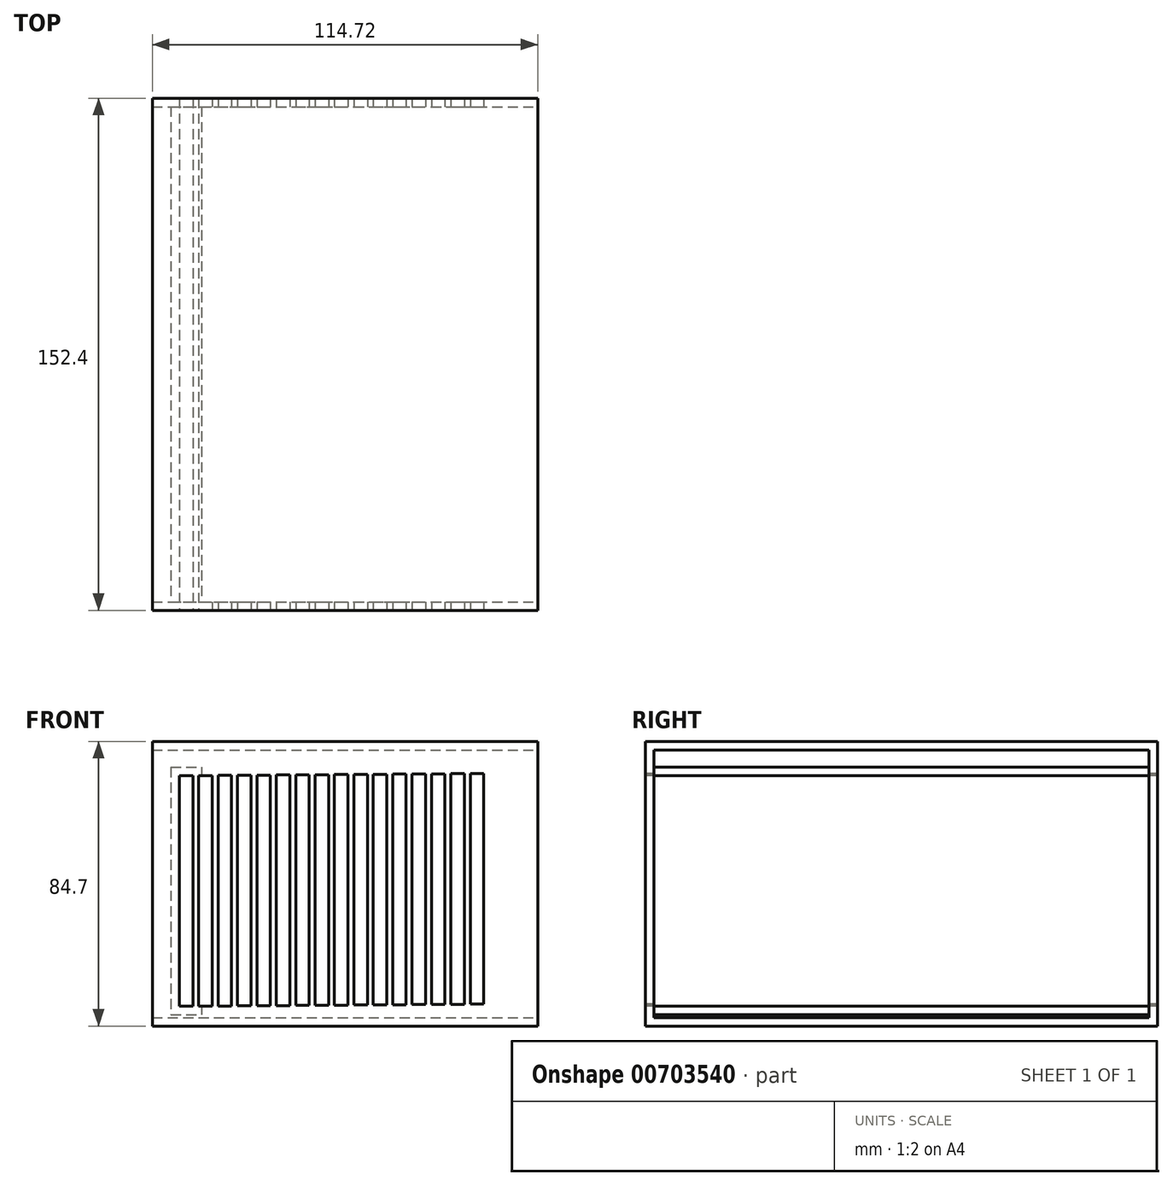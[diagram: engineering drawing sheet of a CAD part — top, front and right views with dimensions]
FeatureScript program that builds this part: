
annotation { "Feature Type Name" : "Feature", "Feature Type Description" : "" }
export const myFeature = defineFeature(function(context is Context, id is Id, definition is map)
    precondition{}
    {
        {
            var Q0;
            Q0=qCreatedBy(makeId("Front.planeOp"),FACE);
            var sketch = newSketch(context, id + "F0", { "sketchPlane" : qUnion([Q0])});
            skLineSegment(sketch, "E0.bottom", {"start": v(-56.22, 44.16) * mm, "end": v(58.5, 44.16) * mm});
            skLineSegment(sketch, "E0.top", {"start": v(-56.22, -40.54) * mm, "end": v(58.5, -40.54) * mm});
            skLineSegment(sketch, "E0.left", {"start": v(-56.22, 44.16) * mm, "end": v(-56.22, -40.54) * mm});
            skLineSegment(sketch, "E0.right", {"start": v(58.5, 44.16) * mm, "end": v(58.5, -40.54) * mm});
            skSolve(sketch);
        }
        {
            var Q0;
            Q0 = qSketchRegion(id + "F0", true);
            extrude(context, id + "F1", {"entities" : qUnion([Q0]), "depth" : 152.4 * mm, "offsetDistance" : 25.4 * mm});
        }
        {
            var Q0;
            Q0=makeQuery(id+"F1.opExtrude","CAP_FACE",FACE,{"disambiguationData":[OSD([sQuery(id+"F0.wireOp",EDGE,"E0.bottom"),sQuery(id+"F0.wireOp",EDGE,"E0.top"),sQuery(id+"F0.wireOp",EDGE,"E0.left"),sQuery(id+"F0.wireOp",EDGE,"E0.right")])],"isStart":false});
            var sketch = newSketch(context, id + "F2", { "sketchPlane" : qUnion([Q0])});
            skLineSegment(sketch, "E1.bottom", {"start": v(-48.18, 33.97) * mm, "end": v(-44.16, 33.97) * mm});
            skLineSegment(sketch, "E1.top", {"start": v(-48.18, -34.64) * mm, "end": v(-44.16, -34.64) * mm});
            skLineSegment(sketch, "E1.left", {"start": v(-48.18, 33.97) * mm, "end": v(-48.18, -34.64) * mm});
            skLineSegment(sketch, "E1.right", {"start": v(-44.16, 33.97) * mm, "end": v(-44.16, -34.64) * mm});
            skLineSegment(sketch, "E2.bottom", {"start": v(-2.01, 34.3) * mm, "end": v(2.01, 34.3) * mm});
            skLineSegment(sketch, "E2.top", {"start": v(-2.01, -34.3) * mm, "end": v(2.01, -34.3) * mm});
            skLineSegment(sketch, "E2.left", {"start": v(-2.01, 34.3) * mm, "end": v(-2.01, -34.3) * mm});
            skLineSegment(sketch, "E2.right", {"start": v(2.01, 34.3) * mm, "end": v(2.01, -34.3) * mm});
            skLineSegment(sketch, "E3.bottom", {"start": v(-25.1, 34.14) * mm, "end": v(-21.07, 34.14) * mm});
            skLineSegment(sketch, "E3.top", {"start": v(-25.1, -34.48) * mm, "end": v(-21.07, -34.48) * mm});
            skLineSegment(sketch, "E3.left", {"start": v(-25.1, 34.14) * mm, "end": v(-25.1, -34.48) * mm});
            skLineSegment(sketch, "E3.right", {"start": v(-21.07, 34.14) * mm, "end": v(-21.07, -34.48) * mm});
            skLineSegment(sketch, "E4.bottom", {"start": v(21.07, 34.48) * mm, "end": v(25.1, 34.48) * mm});
            skLineSegment(sketch, "E4.top", {"start": v(21.07, -34.14) * mm, "end": v(25.1, -34.14) * mm});
            skLineSegment(sketch, "E4.left", {"start": v(21.07, 34.48) * mm, "end": v(21.07, -34.14) * mm});
            skLineSegment(sketch, "E4.right", {"start": v(25.1, 34.48) * mm, "end": v(25.1, -34.14) * mm});
            skLineSegment(sketch, "E5.bottom", {"start": v(-36.64, 34.06) * mm, "end": v(-32.62, 34.06) * mm});
            skLineSegment(sketch, "E5.top", {"start": v(-36.64, -34.56) * mm, "end": v(-32.62, -34.56) * mm});
            skLineSegment(sketch, "E5.left", {"start": v(-36.64, 34.06) * mm, "end": v(-36.64, -34.56) * mm});
            skLineSegment(sketch, "E5.right", {"start": v(-32.62, 34.06) * mm, "end": v(-32.62, -34.56) * mm});
            skLineSegment(sketch, "E6.bottom", {"start": v(9.53, 34.4) * mm, "end": v(13.55, 34.4) * mm});
            skLineSegment(sketch, "E6.top", {"start": v(9.53, -34.23) * mm, "end": v(13.55, -34.23) * mm});
            skLineSegment(sketch, "E6.left", {"start": v(9.53, 34.4) * mm, "end": v(9.53, -34.23) * mm});
            skLineSegment(sketch, "E6.right", {"start": v(13.55, 34.4) * mm, "end": v(13.55, -34.23) * mm});
            skLineSegment(sketch, "E7.bottom", {"start": v(-13.55, 34.23) * mm, "end": v(-9.53, 34.23) * mm});
            skLineSegment(sketch, "E7.top", {"start": v(-13.55, -34.4) * mm, "end": v(-9.53, -34.4) * mm});
            skLineSegment(sketch, "E7.left", {"start": v(-13.55, 34.23) * mm, "end": v(-13.55, -34.4) * mm});
            skLineSegment(sketch, "E7.right", {"start": v(-9.53, 34.23) * mm, "end": v(-9.53, -34.4) * mm});
            skLineSegment(sketch, "E8.bottom", {"start": v(32.62, 34.56) * mm, "end": v(36.64, 34.56) * mm});
            skLineSegment(sketch, "E8.top", {"start": v(32.62, -34.06) * mm, "end": v(36.64, -34.06) * mm});
            skLineSegment(sketch, "E8.left", {"start": v(32.62, 34.56) * mm, "end": v(32.62, -34.06) * mm});
            skLineSegment(sketch, "E8.right", {"start": v(36.64, 34.56) * mm, "end": v(36.64, -34.06) * mm});
            skLineSegment(sketch, "E9.bottom", {"start": v(-42.4, 34.02) * mm, "end": v(-38.39, 34.02) * mm});
            skLineSegment(sketch, "E9.top", {"start": v(-42.4, -34.6) * mm, "end": v(-38.39, -34.6) * mm});
            skLineSegment(sketch, "E9.left", {"start": v(-42.4, 34.02) * mm, "end": v(-42.4, -34.6) * mm});
            skLineSegment(sketch, "E9.right", {"start": v(-38.39, 34.02) * mm, "end": v(-38.39, -34.6) * mm});
            skLineSegment(sketch, "E10.bottom", {"start": v(3.76, 34.35) * mm, "end": v(7.78, 34.35) * mm});
            skLineSegment(sketch, "E10.top", {"start": v(3.76, -34.27) * mm, "end": v(7.78, -34.27) * mm});
            skLineSegment(sketch, "E10.left", {"start": v(3.76, 34.35) * mm, "end": v(3.76, -34.27) * mm});
            skLineSegment(sketch, "E10.right", {"start": v(7.78, 34.35) * mm, "end": v(7.78, -34.27) * mm});
            skLineSegment(sketch, "E11.bottom", {"start": v(-19.32, 34.18) * mm, "end": v(-15.3, 34.18) * mm});
            skLineSegment(sketch, "E11.top", {"start": v(-19.32, -34.43) * mm, "end": v(-15.3, -34.43) * mm});
            skLineSegment(sketch, "E11.left", {"start": v(-19.32, 34.18) * mm, "end": v(-19.32, -34.43) * mm});
            skLineSegment(sketch, "E11.right", {"start": v(-15.3, 34.18) * mm, "end": v(-15.3, -34.43) * mm});
            skLineSegment(sketch, "E12.bottom", {"start": v(26.85, 34.52) * mm, "end": v(30.87, 34.52) * mm});
            skLineSegment(sketch, "E12.top", {"start": v(26.85, -34.1) * mm, "end": v(30.87, -34.1) * mm});
            skLineSegment(sketch, "E12.left", {"start": v(26.85, 34.52) * mm, "end": v(26.85, -34.1) * mm});
            skLineSegment(sketch, "E12.right", {"start": v(30.87, 34.52) * mm, "end": v(30.87, -34.1) * mm});
            skLineSegment(sketch, "E13.bottom", {"start": v(-30.87, 34.1) * mm, "end": v(-26.85, 34.1) * mm});
            skLineSegment(sketch, "E13.top", {"start": v(-30.87, -34.52) * mm, "end": v(-26.85, -34.52) * mm});
            skLineSegment(sketch, "E13.left", {"start": v(-30.87, 34.1) * mm, "end": v(-30.87, -34.52) * mm});
            skLineSegment(sketch, "E13.right", {"start": v(-26.85, 34.1) * mm, "end": v(-26.85, -34.52) * mm});
            skLineSegment(sketch, "E14.bottom", {"start": v(15.3, 34.43) * mm, "end": v(19.32, 34.43) * mm});
            skLineSegment(sketch, "E14.top", {"start": v(15.3, -34.18) * mm, "end": v(19.32, -34.18) * mm});
            skLineSegment(sketch, "E14.left", {"start": v(15.3, 34.43) * mm, "end": v(15.3, -34.18) * mm});
            skLineSegment(sketch, "E14.right", {"start": v(19.32, 34.43) * mm, "end": v(19.32, -34.18) * mm});
            skLineSegment(sketch, "E15.bottom", {"start": v(-7.78, 34.27) * mm, "end": v(-3.76, 34.27) * mm});
            skLineSegment(sketch, "E15.top", {"start": v(-7.78, -34.35) * mm, "end": v(-3.76, -34.35) * mm});
            skLineSegment(sketch, "E15.left", {"start": v(-7.78, 34.27) * mm, "end": v(-7.78, -34.35) * mm});
            skLineSegment(sketch, "E15.right", {"start": v(-3.76, 34.27) * mm, "end": v(-3.76, -34.35) * mm});
            skLineSegment(sketch, "E16.bottom", {"start": v(38.39, 34.6) * mm, "end": v(42.4, 34.6) * mm});
            skLineSegment(sketch, "E16.top", {"start": v(38.39, -34.02) * mm, "end": v(42.4, -34.02) * mm});
            skLineSegment(sketch, "E16.left", {"start": v(38.39, 34.6) * mm, "end": v(38.39, -34.02) * mm});
            skLineSegment(sketch, "E16.right", {"start": v(42.4, 34.6) * mm, "end": v(42.4, -34.02) * mm});
            skSolve(sketch);
        }
        {
            var Q0;
            Q0=makeQuery(id+"F2.imprint","IMPRINT",FACE,{"disambiguationData":[TD([[makeQuery(id+"F2.imprint","IMPRINT",EDGE,{"derivedFrom":sQuery(id+"F2.wireOp",EDGE,"E1.bottom")}),-1.0]])]});
            extrude(context, id + "F3", {"entities" : qUnion([Q0]), "operationType" : NewBodyOperationType.REMOVE, "oppositeDirection" : true, "depth" : 152.4 * mm, "offsetDistance" : 25.4 * mm});
        }
        {
            var Q0;
            Q0=makeQuery(id+"F1.opExtrude","SWEPT_FACE",FACE,{"disambiguationData":[OSD([sQuery(id+"F0.wireOp",EDGE,"E0.left")])]});
            var Q1;
            Q1=makeQuery(id+"F1.opExtrude","SWEPT_FACE",FACE,{"disambiguationData":[OSD([sQuery(id+"F0.wireOp",EDGE,"E0.right")])]});
            shell(context, id + "F4", {"entities" : qUnion([Q0, Q1]), "thickness" : 2.54 * mm});
        }
        {
            var Q0;
            Q0=makeQuery(id+"F2.imprint","IMPRINT",FACE,{"disambiguationData":[TD([[makeQuery(id+"F2.imprint","IMPRINT",EDGE,{"derivedFrom":sQuery(id+"F2.wireOp",EDGE,"E2.bottom")}),-1.0]])]});
            extrude(context, id + "F5", {"entities" : qUnion([Q0]), "operationType" : NewBodyOperationType.REMOVE, "endBound" : BoundingType.THROUGH_ALL, "oppositeDirection" : true, "depth" : 25.4 * mm, "offsetDistance" : 25.4 * mm});
        }
        {
            var Q0;
            Q0=makeQuery(id+"F2.imprint","IMPRINT",FACE,{"disambiguationData":[TD([[makeQuery(id+"F2.imprint","IMPRINT",EDGE,{"derivedFrom":sQuery(id+"F2.wireOp",EDGE,"E3.bottom")}),-1.0]])]});
            var Q1;
            Q1=makeQuery(id+"F2.imprint","IMPRINT",FACE,{"disambiguationData":[TD([[makeQuery(id+"F2.imprint","IMPRINT",EDGE,{"derivedFrom":sQuery(id+"F2.wireOp",EDGE,"E4.bottom")}),-1.0]])]});
            var Q2;
            Q2=sQuery(id+"F2.wireOp",EDGE,"E3.bottom");
            var Q3;
            Q3=sQuery(id+"F2.wireOp",EDGE,"E3.top");
            var Q4;
            Q4=sQuery(id+"F2.wireOp",EDGE,"E3.left");
            var Q5;
            Q5=sQuery(id+"F2.wireOp",EDGE,"E3.right");
            var Q6;
            Q6=sQuery(id+"F2.wireOp",EDGE,"E4.bottom");
            var Q7;
            Q7=sQuery(id+"F2.wireOp",EDGE,"E4.top");
            var Q8;
            Q8=sQuery(id+"F2.wireOp",EDGE,"E4.left");
            var Q9;
            Q9=sQuery(id+"F2.wireOp",EDGE,"E4.right");
            extrude(context, id + "F6", {"entities" : qUnion([Q0, Q1]), "operationType" : NewBodyOperationType.REMOVE, "surfaceEntities" : qUnion([Q2, Q3, Q4, Q5, Q6, Q7, Q8, Q9]), "endBound" : BoundingType.THROUGH_ALL, "oppositeDirection" : true, "depth" : 25.4 * mm, "offsetDistance" : 25.4 * mm});
        }
        {
            var Q0;
            Q0=makeQuery(id+"F2.imprint","IMPRINT",FACE,{"disambiguationData":[TD([[makeQuery(id+"F2.imprint","IMPRINT",EDGE,{"derivedFrom":sQuery(id+"F2.wireOp",EDGE,"E5.bottom")}),-1.0]])]});
            var Q1;
            Q1=makeQuery(id+"F2.imprint","IMPRINT",FACE,{"disambiguationData":[TD([[makeQuery(id+"F2.imprint","IMPRINT",EDGE,{"derivedFrom":sQuery(id+"F2.wireOp",EDGE,"E7.bottom")}),-1.0]])]});
            var Q2;
            Q2=makeQuery(id+"F2.imprint","IMPRINT",FACE,{"disambiguationData":[TD([[makeQuery(id+"F2.imprint","IMPRINT",EDGE,{"derivedFrom":sQuery(id+"F2.wireOp",EDGE,"E6.bottom")}),-1.0]])]});
            var Q3;
            Q3=makeQuery(id+"F2.imprint","IMPRINT",FACE,{"disambiguationData":[TD([[makeQuery(id+"F2.imprint","IMPRINT",EDGE,{"derivedFrom":sQuery(id+"F2.wireOp",EDGE,"E8.bottom")}),-1.0]])]});
            extrude(context, id + "F7", {"entities" : qUnion([Q0, Q1, Q2, Q3]), "operationType" : NewBodyOperationType.REMOVE, "endBound" : BoundingType.THROUGH_ALL, "oppositeDirection" : true, "depth" : 25.4 * mm, "offsetDistance" : 25.4 * mm});
        }
        {
            var Q0;
            Q0=makeQuery(id+"F2.imprint","IMPRINT",FACE,{"disambiguationData":[TD([[makeQuery(id+"F2.imprint","IMPRINT",EDGE,{"derivedFrom":sQuery(id+"F2.wireOp",EDGE,"E9.bottom")}),-1.0]])]});
            var Q1;
            Q1=makeQuery(id+"F2.imprint","IMPRINT",FACE,{"disambiguationData":[TD([[makeQuery(id+"F2.imprint","IMPRINT",EDGE,{"derivedFrom":sQuery(id+"F2.wireOp",EDGE,"E13.bottom")}),-1.0]])]});
            var Q2;
            Q2=makeQuery(id+"F2.imprint","IMPRINT",FACE,{"disambiguationData":[TD([[makeQuery(id+"F2.imprint","IMPRINT",EDGE,{"derivedFrom":sQuery(id+"F2.wireOp",EDGE,"E11.bottom")}),-1.0]])]});
            var Q3;
            Q3=makeQuery(id+"F2.imprint","IMPRINT",FACE,{"disambiguationData":[TD([[makeQuery(id+"F2.imprint","IMPRINT",EDGE,{"derivedFrom":sQuery(id+"F2.wireOp",EDGE,"E15.bottom")}),-1.0]])]});
            var Q4;
            Q4=makeQuery(id+"F2.imprint","IMPRINT",FACE,{"disambiguationData":[TD([[makeQuery(id+"F2.imprint","IMPRINT",EDGE,{"derivedFrom":sQuery(id+"F2.wireOp",EDGE,"E10.bottom")}),-1.0]])]});
            var Q5;
            Q5=makeQuery(id+"F2.imprint","IMPRINT",FACE,{"disambiguationData":[TD([[makeQuery(id+"F2.imprint","IMPRINT",EDGE,{"derivedFrom":sQuery(id+"F2.wireOp",EDGE,"E14.bottom")}),-1.0]])]});
            var Q6;
            Q6=makeQuery(id+"F2.imprint","IMPRINT",FACE,{"disambiguationData":[TD([[makeQuery(id+"F2.imprint","IMPRINT",EDGE,{"derivedFrom":sQuery(id+"F2.wireOp",EDGE,"E12.bottom")}),-1.0]])]});
            var Q7;
            Q7=makeQuery(id+"F2.imprint","IMPRINT",FACE,{"disambiguationData":[TD([[makeQuery(id+"F2.imprint","IMPRINT",EDGE,{"derivedFrom":sQuery(id+"F2.wireOp",EDGE,"E16.bottom")}),-1.0]])]});
            var Q8;
            Q8=sQuery(id+"F2.wireOp",EDGE,"E9.bottom");
            var Q9;
            Q9=sQuery(id+"F2.wireOp",EDGE,"E9.top");
            var Q10;
            Q10=sQuery(id+"F2.wireOp",EDGE,"E9.left");
            var Q11;
            Q11=sQuery(id+"F2.wireOp",EDGE,"E9.right");
            var Q12;
            Q12=sQuery(id+"F2.wireOp",EDGE,"E10.bottom");
            var Q13;
            Q13=sQuery(id+"F2.wireOp",EDGE,"E10.top");
            var Q14;
            Q14=sQuery(id+"F2.wireOp",EDGE,"E10.left");
            var Q15;
            Q15=sQuery(id+"F2.wireOp",EDGE,"E10.right");
            var Q16;
            Q16=sQuery(id+"F2.wireOp",EDGE,"E11.bottom");
            var Q17;
            Q17=sQuery(id+"F2.wireOp",EDGE,"E11.top");
            var Q18;
            Q18=sQuery(id+"F2.wireOp",EDGE,"E11.left");
            var Q19;
            Q19=sQuery(id+"F2.wireOp",EDGE,"E11.right");
            var Q20;
            Q20=sQuery(id+"F2.wireOp",EDGE,"E12.bottom");
            var Q21;
            Q21=sQuery(id+"F2.wireOp",EDGE,"E12.top");
            var Q22;
            Q22=sQuery(id+"F2.wireOp",EDGE,"E12.left");
            var Q23;
            Q23=sQuery(id+"F2.wireOp",EDGE,"E12.right");
            var Q24;
            Q24=sQuery(id+"F2.wireOp",EDGE,"E13.bottom");
            var Q25;
            Q25=sQuery(id+"F2.wireOp",EDGE,"E13.top");
            var Q26;
            Q26=sQuery(id+"F2.wireOp",EDGE,"E13.left");
            var Q27;
            Q27=sQuery(id+"F2.wireOp",EDGE,"E13.right");
            var Q28;
            Q28=sQuery(id+"F2.wireOp",EDGE,"E14.bottom");
            var Q29;
            Q29=sQuery(id+"F2.wireOp",EDGE,"E14.top");
            var Q30;
            Q30=sQuery(id+"F2.wireOp",EDGE,"E14.left");
            var Q31;
            Q31=sQuery(id+"F2.wireOp",EDGE,"E14.right");
            var Q32;
            Q32=sQuery(id+"F2.wireOp",EDGE,"E15.bottom");
            var Q33;
            Q33=sQuery(id+"F2.wireOp",EDGE,"E15.top");
            var Q34;
            Q34=sQuery(id+"F2.wireOp",EDGE,"E15.left");
            var Q35;
            Q35=sQuery(id+"F2.wireOp",EDGE,"E15.right");
            var Q36;
            Q36=sQuery(id+"F2.wireOp",EDGE,"E16.bottom");
            var Q37;
            Q37=sQuery(id+"F2.wireOp",EDGE,"E16.top");
            var Q38;
            Q38=sQuery(id+"F2.wireOp",EDGE,"E16.left");
            var Q39;
            Q39=sQuery(id+"F2.wireOp",EDGE,"E16.right");
            extrude(context, id + "F8", {"entities" : qUnion([Q0, Q1, Q2, Q3, Q4, Q5, Q6, Q7]), "operationType" : NewBodyOperationType.REMOVE, "surfaceEntities" : qUnion([Q8, Q9, Q10, Q11, Q12, Q13, Q14, Q15, Q16, Q17, Q18, Q19, Q20, Q21, Q22, Q23, Q24, Q25, Q26, Q27, Q28, Q29, Q30, Q31, Q32, Q33, Q34, Q35, Q36, Q37, Q38, Q39]), "endBound" : BoundingType.THROUGH_ALL, "oppositeDirection" : true, "depth" : 25.4 * mm, "offsetDistance" : 25.4 * mm});
        }
    });
